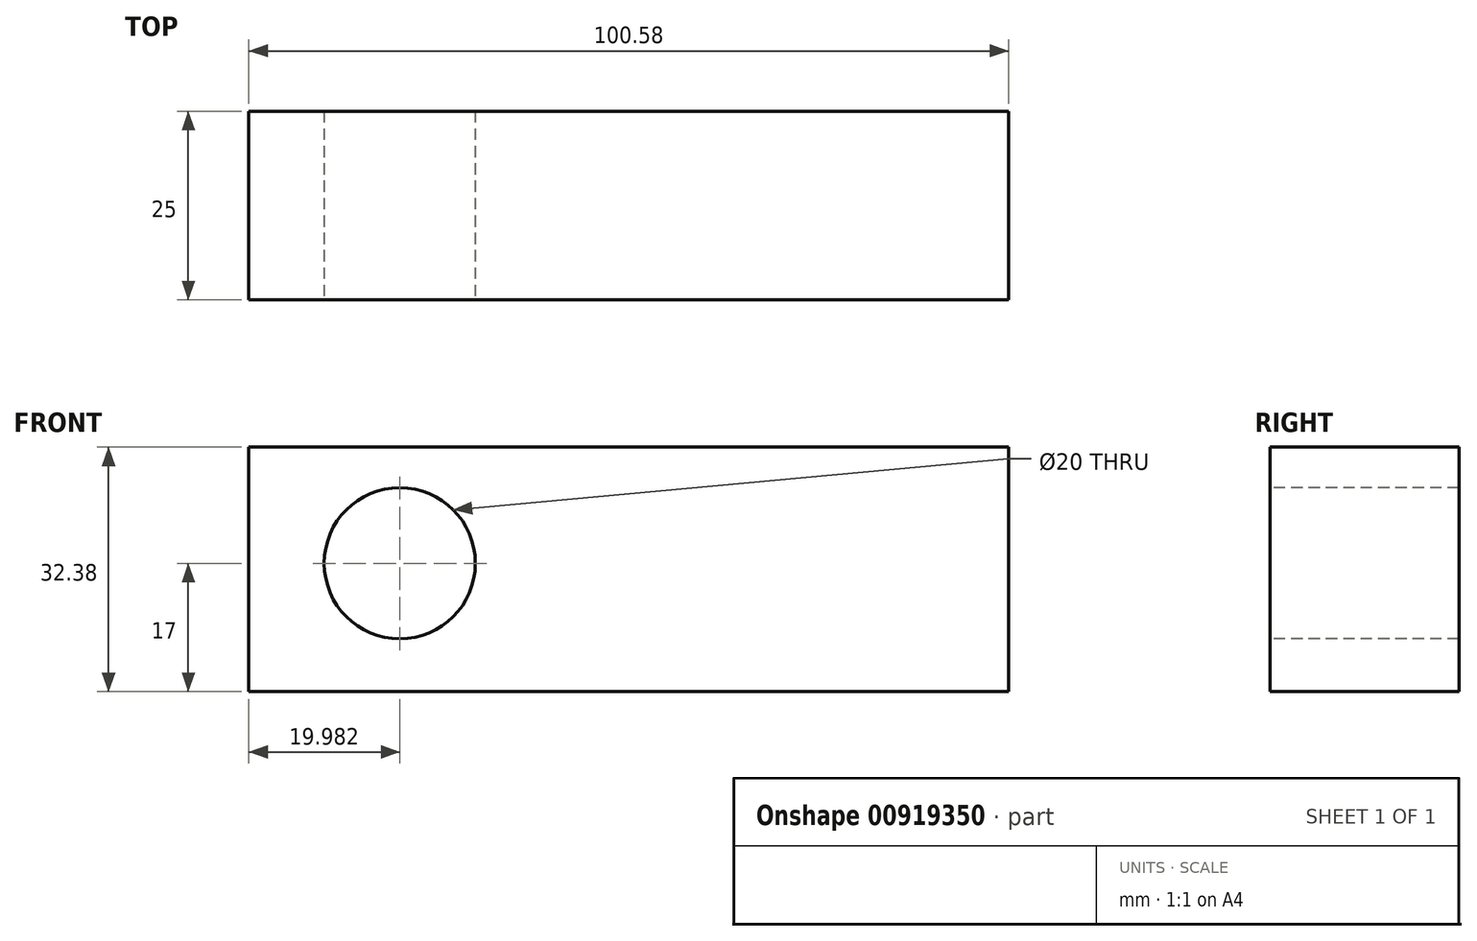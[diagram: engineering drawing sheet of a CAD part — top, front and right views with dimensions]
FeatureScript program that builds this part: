
annotation { "Feature Type Name" : "Feature", "Feature Type Description" : "" }
export const myFeature = defineFeature(function(context is Context, id is Id, definition is map)
    precondition{}
    {
        {
            var Q0;
            Q0=qCreatedBy(makeId("Front.planeOp"),FACE);
            var sketch = newSketch(context, id + "F0", { "sketchPlane" : qUnion([Q0])});
            skLineSegment(sketch, "E0.bottom", {"start": v(-50.3, 32.38) * mm, "end": v(50.3, 32.38) * mm});
            skLineSegment(sketch, "E0.top", {"start": v(-50.3, 0) * mm, "end": v(50.3, 0) * mm});
            skLineSegment(sketch, "E0.left", {"start": v(-50.3, 32.38) * mm, "end": v(-50.3, 0) * mm});
            skLineSegment(sketch, "E0.right", {"start": v(50.3, 32.38) * mm, "end": v(50.3, 0) * mm});
            skSolve(sketch);
        }
        {
            var Q0;
            Q0 = qSketchRegion(id + "F0", true);
            extrude(context, id + "F1", {"entities" : qUnion([Q0]), "depth" : 25 * mm, "offsetDistance" : 25 * mm});
        }
        {
            var Q0;
            Q0=makeQuery(id+"F1.opExtrude","CAP_FACE",FACE,{"disambiguationData":[OSD([sQuery(id+"F0.wireOp",EDGE,"E0.bottom"),sQuery(id+"F0.wireOp",EDGE,"E0.top"),sQuery(id+"F0.wireOp",EDGE,"E0.left"),sQuery(id+"F0.wireOp",EDGE,"E0.right")])],"isStart":false});
            var sketch = newSketch(context, id + "F2", { "sketchPlane" : qUnion([Q0])});
            skCircle(sketch, "E1", {"center": v(-30.3, 17) * mm, "radius": 10 * mm});
            skSolve(sketch);
        }
        {
            var Q0;
            Q0=makeQuery(id+"F2.imprint","IMPRINT",FACE,{"disambiguationData":[TD([[makeQuery(id+"F2.imprint","IMPRINT",EDGE,{"derivedFrom":sQuery(id+"F2.wireOp",EDGE,"E1")}),1.0]])]});
            var Q1;
            Q1=sQuery(id+"F2.wireOp",EDGE,"E1");
            extrude(context, id + "F3", {"entities" : qUnion([Q0]), "operationType" : NewBodyOperationType.REMOVE, "surfaceEntities" : qUnion([Q1]), "oppositeDirection" : true, "depth" : 38.7 * mm, "offsetDistance" : 25 * mm});
        }
    });
